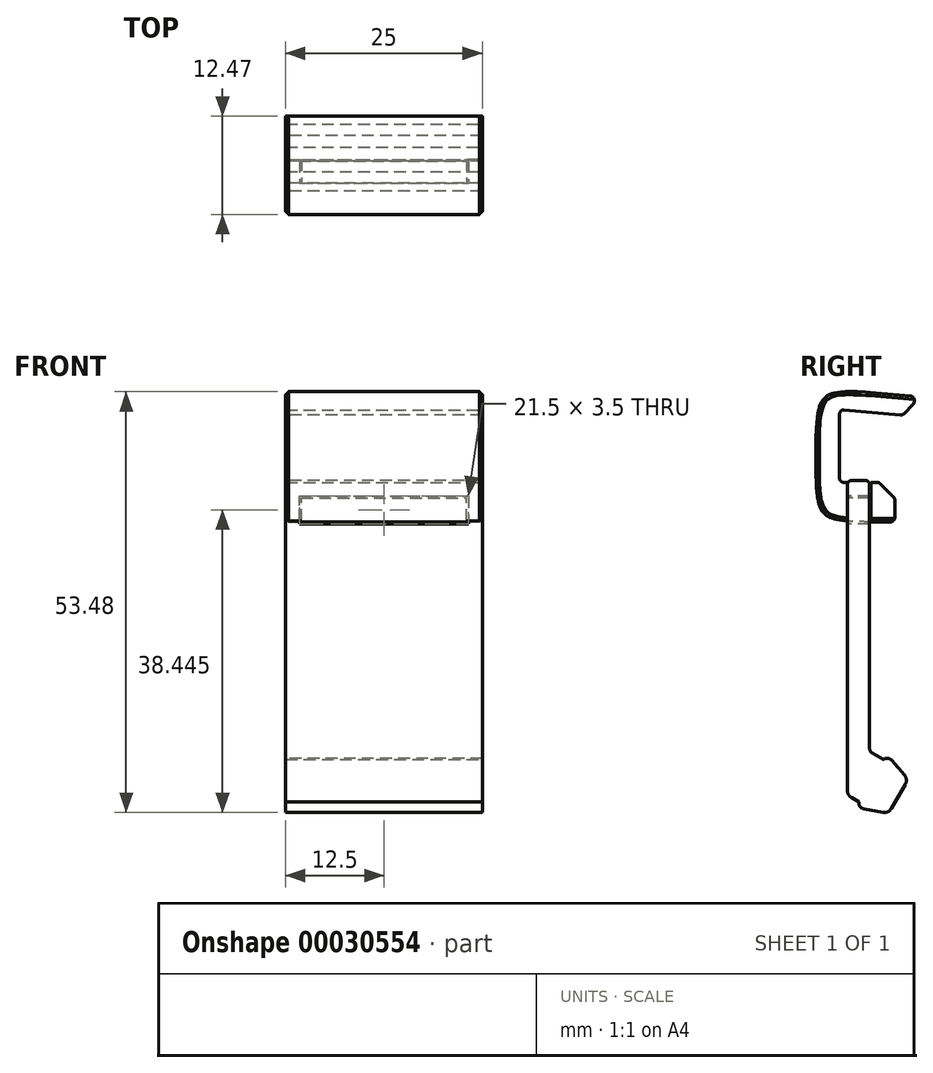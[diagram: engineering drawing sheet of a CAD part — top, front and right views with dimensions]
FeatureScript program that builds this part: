
annotation { "Feature Type Name" : "Feature", "Feature Type Description" : "" }
export const myFeature = defineFeature(function(context is Context, id is Id, definition is map)
    precondition{}
    {
        {
            var Q0;
            Q0=qCreatedBy(makeId("Right.planeOp"),FACE);
            var sketch = newSketch(context, id + "F0", { "sketchPlane" : qUnion([Q0])});
            skLineSegment(sketch, "E0", {"start": v(0, 4.62) * mm, "end": v(0, -4.62) * mm});
            skLineSegment(sketch, "E1", {"start": v(0, -4.62) * mm, "end": v(5, -4.62) * mm});
            skLineSegment(sketch, "E2", {"start": v(5, -4.62) * mm, "end": v(7, -6.62) * mm});
            skLineSegment(sketch, "E3", {"start": v(7, -6.62) * mm, "end": v(7, -9.62) * mm});
            skLineSegment(sketch, "E4", {"start": v(7, -9.62) * mm, "end": v(-3, -9.62) * mm});
            skLineSegment(sketch, "E5", {"start": v(-3, -9.63) * mm, "end": v(-3, 7.4) * mm});
            skLineSegment(sketch, "E6", {"start": v(-3, 7.4) * mm, "end": v(9.47, 6.3) * mm});
            skLineSegment(sketch, "E7", {"start": v(9.47, 6.3) * mm, "end": v(9.47, 5.43) * mm});
            skLineSegment(sketch, "E8", {"start": v(9.47, 5.43) * mm, "end": v(7.97, 3.93) * mm});
            skLineSegment(sketch, "E9", {"start": v(7.97, 3.93) * mm, "end": v(0, 4.63) * mm});
            skLineSegment(sketch, "E10", {"start": v(7.97, 3.93) * mm, "end": v(9.47, 3.93) * mm, "construction": true});
            skLineSegment(sketch, "E11", {"start": v(9.47, 3.93) * mm, "end": v(9.47, 5.43) * mm, "construction": true});
            skLineSegment(sketch, "E12", {"start": v(5, -4.62) * mm, "end": v(7, -4.62) * mm, "construction": true});
            skLineSegment(sketch, "E13", {"start": v(7, -4.62) * mm, "end": v(7, -6.62) * mm, "construction": true});
            skSolve(sketch);
        }
        {
            var Q0;
            Q0 = qSketchRegion(id + "F0", true);
            extrude(context, id + "F1", {"entities" : qUnion([Q0]), "depth" : 25 * mm});
        }
        {
            var Q0;
            Q0=makeQuery(id+"F1.opExtrude","SWEPT_EDGE",EDGE,{"disambiguationData":[OSD([sQuery(id+"F0.wireOp",EDGE,"E5"),sQuery(id+"F0.wireOp",EDGE,"E6")])]});
            var Q1;
            Q1=makeQuery(id+"F1.opExtrude","SWEPT_EDGE",EDGE,{"disambiguationData":[OSD([sQuery(id+"F0.wireOp",EDGE,"E4"),sQuery(id+"F0.wireOp",EDGE,"E5")])]});
            fillet(context, id + "F2", {"entities" : qUnion([Q0, Q1]), "radius" : 7 * mm, "tangentPropagation" : true, "rho" : .7, "crossSection" : FilletCrossSection.CONIC, "allowEdgeOverflow" : false});
        }
        {
            var Q0;
            Q0=makeQuery(id+"F1.opExtrude","SWEPT_EDGE",EDGE,{"disambiguationData":[OSD([sQuery(id+"F0.wireOp",EDGE,"E0"),sQuery(id+"F0.wireOp",EDGE,"E9")])]});
            var Q1;
            Q1=makeQuery(id+"F1.opExtrude","SWEPT_EDGE",EDGE,{"disambiguationData":[OSD([sQuery(id+"F0.wireOp",EDGE,"E0"),sQuery(id+"F0.wireOp",EDGE,"E1")])]});
            var Q2;
            Q2=makeQuery(id+"F1.opExtrude","SWEPT_EDGE",EDGE,{"disambiguationData":[OSD([sQuery(id+"F0.wireOp",EDGE,"E6"),sQuery(id+"F0.wireOp",EDGE,"E7")])]});
            var Q3;
            Q3=makeQuery(id+"F1.opExtrude","SWEPT_EDGE",EDGE,{"disambiguationData":[OSD([sQuery(id+"F0.wireOp",EDGE,"E7"),sQuery(id+"F0.wireOp",EDGE,"E8")])]});
            var Q4;
            Q4=makeQuery(id+"F1.opExtrude","SWEPT_EDGE",EDGE,{"disambiguationData":[OSD([sQuery(id+"F0.wireOp",EDGE,"E8"),sQuery(id+"F0.wireOp",EDGE,"E9")])]});
            var Q5;
            Q5=makeQuery(id+"F1.opExtrude","SWEPT_EDGE",EDGE,{"disambiguationData":[OSD([sQuery(id+"F0.wireOp",EDGE,"E1"),sQuery(id+"F0.wireOp",EDGE,"E2")])]});
            var Q6;
            Q6=makeQuery(id+"F1.opExtrude","SWEPT_EDGE",EDGE,{"disambiguationData":[OSD([sQuery(id+"F0.wireOp",EDGE,"E2"),sQuery(id+"F0.wireOp",EDGE,"E3")])]});
            var Q7;
            Q7=makeQuery(id+"F1.opExtrude","SWEPT_EDGE",EDGE,{"disambiguationData":[OSD([sQuery(id+"F0.wireOp",EDGE,"E3"),sQuery(id+"F0.wireOp",EDGE,"E4")])]});
            fillet(context, id + "F3", {"entities" : qUnion([Q0, Q1, Q2, Q3, Q4, Q5, Q6, Q7]), "radius" : .5 * mm, "tangentPropagation" : true, "allowEdgeOverflow" : false});
        }
        {
            var Q0;
            Q0=makeQuery(id+"F1.opExtrude","CAP_FACE",FACE,{"disambiguationData":[OSD([sQuery(id+"F0.wireOp",EDGE,"E0"),sQuery(id+"F0.wireOp",EDGE,"E1"),sQuery(id+"F0.wireOp",EDGE,"E2"),sQuery(id+"F0.wireOp",EDGE,"E3"),sQuery(id+"F0.wireOp",EDGE,"E4"),sQuery(id+"F0.wireOp",EDGE,"E5"),sQuery(id+"F0.wireOp",EDGE,"E6"),sQuery(id+"F0.wireOp",EDGE,"E7"),sQuery(id+"F0.wireOp",EDGE,"E8"),sQuery(id+"F0.wireOp",EDGE,"E9")])],"isStart":false});
            var sketch = newSketch(context, id + "F4", { "sketchPlane" : qUnion([Q0])});
            skLineSegment(sketch, "E14.bottom", {"start": v(1, -4.62) * mm, "end": v(4, -4.62) * mm});
            skLineSegment(sketch, "E14.top", {"start": v(1, -6.62) * mm, "end": v(4, -6.62) * mm});
            skLineSegment(sketch, "E14.left", {"start": v(1, -4.62) * mm, "end": v(1, -6.62) * mm});
            skLineSegment(sketch, "E14.right", {"start": v(4, -4.62) * mm, "end": v(4, -6.62) * mm});
            skSolve(sketch);
        }
        {
            var Q0;
            Q0 = qSketchRegion(id + "F4", true);
            extrude(context, id + "F5", {"entities" : qUnion([Q0]), "operationType" : NewBodyOperationType.REMOVE, "endBound" : BoundingType.THROUGH_ALL, "oppositeDirection" : true, "depth" : 25 * mm});
        }
        {
            var Q0;
            Q0=makeQuery(id+"F5.boolean.opBoolean","COPY",FACE,{"derivedFrom":makeQuery(id+"F5.opExtrude","SWEPT_FACE",FACE,{"disambiguationData":[OSD([sQuery(id+"F4.wireOp",EDGE,"E14.top")])]})});
            var sketch = newSketch(context, id + "F6", { "sketchPlane" : qUnion([Q0])});
            skLineSegment(sketch, "E15.bottom", {"start": v(25, 4) * mm, "end": v(23, 4) * mm});
            skLineSegment(sketch, "E15.top", {"start": v(25, 1) * mm, "end": v(23, 1) * mm});
            skLineSegment(sketch, "E15.left", {"start": v(25, 4) * mm, "end": v(25, 1) * mm});
            skLineSegment(sketch, "E15.right", {"start": v(23, 4) * mm, "end": v(23, 1) * mm});
            skLineSegment(sketch, "E16.bottom", {"start": v(0, 1) * mm, "end": v(2, 1) * mm});
            skLineSegment(sketch, "E16.top", {"start": v(0, 4) * mm, "end": v(2, 4) * mm});
            skLineSegment(sketch, "E16.left", {"start": v(0, 4) * mm, "end": v(0, 1) * mm});
            skLineSegment(sketch, "E16.right", {"start": v(2, 4) * mm, "end": v(2, 1) * mm});
            skSolve(sketch);
        }
        {
            var Q0;
            Q0 = qSketchRegion(id + "F6", true);
            extrude(context, id + "F7", {"entities" : qUnion([Q0]), "operationType" : NewBodyOperationType.REMOVE, "endBound" : BoundingType.UP_TO_NEXT, "oppositeDirection" : true, "depth" : 25 * mm});
        }
        {
            var Q0;
            Q0=makeQuery(id+"F7.boolean.opBoolean","MERGE",FACE,{"derivedFrom":[makeQuery(id+"F5.boolean.opBoolean","COPY",FACE,{"derivedFrom":makeQuery(id+"F5.opExtrude","SWEPT_FACE",FACE,{"disambiguationData":[OSD([sQuery(id+"F4.wireOp",EDGE,"E14.left")])]})}),makeQuery(id+"F5.boolean.opBoolean","COPY",FACE,{"derivedFrom":makeQuery(id+"F5.opExtrude","SWEPT_FACE",FACE,{"disambiguationData":[OSD([sQuery(id+"F4.wireOp",EDGE,"d3d7cda7-cd1c-4aa4-936c-d04dcb39f244.right")])]})}),makeQuery(id+"F7.opExtrude","SWEPT_FACE",FACE,{"disambiguationData":[OSD([sQuery(id+"F6.wireOp",EDGE,"E15.bottom")])]}),makeQuery(id+"F7.opExtrude","SWEPT_FACE",FACE,{"disambiguationData":[OSD([sQuery(id+"F6.wireOp",EDGE,"E16.bottom")])]})]});
            cPlane(context, id + "F8", {"entities" : qUnion([Q0]), "cplaneType" : CPlaneType.OFFSET, "offset" : 0 * mm, "width" : 150 * mm, "height" : 150 * mm});
        }
        {
            var Q0;
            Q0=qCreatedBy(id+"F8.planeOp",FACE);
            var sketch = newSketch(context, id + "F9", { "sketchPlane" : qUnion([Q0])});
            skLineSegment(sketch, "E17.bottom", {"start": v(-25, -4.37) * mm, "end": v(0, -4.37) * mm});
            skLineSegment(sketch, "E17.top", {"start": v(-25, -44.38) * mm, "end": v(0, -44.38) * mm});
            skLineSegment(sketch, "E17.left", {"start": v(-25, -4.38) * mm, "end": v(-25, -44.38) * mm});
            skLineSegment(sketch, "E17.right", {"start": v(0, -4.37) * mm, "end": v(0, -44.38) * mm});
            skLineSegment(sketch, "E18.1", {"start": v(-2, -6.62) * mm, "end": v(-23, -6.62) * mm, "construction": true});
            skLineSegment(sketch, "E18.2", {"start": v(-2, -6.63) * mm, "end": v(-2, -6.63) * mm});
            skLineSegment(sketch, "E19", {"start": v(-23, -6.63) * mm, "end": v(-23, -9.63) * mm, "construction": true});
            skLineSegment(sketch, "E20", {"start": v(-23, -9.63) * mm, "end": v(-2, -9.63) * mm, "construction": true});
            skLineSegment(sketch, "E21", {"start": v(-2, -9.63) * mm, "end": v(-2, -6.62) * mm, "construction": true});
            skLineSegment(sketch, "E22.0", {"start": v(-1.75, -6.37) * mm, "end": v(-23.25, -6.37) * mm});
            skLineSegment(sketch, "E22.1", {"start": v(-1.75, -9.88) * mm, "end": v(-1.75, -6.37) * mm});
            skLineSegment(sketch, "E22.2", {"start": v(-23.25, -9.88) * mm, "end": v(-1.75, -9.88) * mm});
            skLineSegment(sketch, "E22.3", {"start": v(-23.25, -6.37) * mm, "end": v(-23.25, -9.88) * mm});
            skSolve(sketch);
        }
        {
            var Q0;
            Q0 = qSketchRegion(id + "F9", true);
            extrude(context, id + "F10", {"entities" : qUnion([Q0]), "depth" : 2.8 * mm});
        }
        {
            var Q0;
            Q0=makeQuery(id+"F10.opExtrude","CAP_EDGE",EDGE,{"disambiguationData":[OSD([sQuery(id+"F9.wireOp",EDGE,"E17.bottom")])],"isStart":false});
            var Q1;
            Q1=makeQuery(id+"F10.opExtrude","CAP_EDGE",EDGE,{"disambiguationData":[OSD([sQuery(id+"F9.wireOp",EDGE,"E17.bottom")])],"isStart":true});
            fillet(context, id + "F11", {"entities" : qUnion([Q0, Q1]), "radius" : .5 * mm, "tangentPropagation" : true, "allowEdgeOverflow" : false});
        }
        {
            var Q0;
            Q0=makeQuery(id+"F10.opExtrude","SWEPT_FACE",FACE,{"disambiguationData":[OSD([sQuery(id+"F9.wireOp",EDGE,"E17.left")])]});
            var sketch = newSketch(context, id + "F12", { "sketchPlane" : qUnion([Q0])});
            skLineSegment(sketch, "E23", {"start": v(5.93, -39.14) * mm, "end": v(8.7, -42.35) * mm});
            skLineSegment(sketch, "E24", {"start": v(8.7, -42.35) * mm, "end": v(6.2, -46.68) * mm});
            skLineSegment(sketch, "E25", {"start": v(6.2, -46.68) * mm, "end": v(2.03, -45.9) * mm});
            skLineSegment(sketch, "E26", {"start": v(2.03, -45.9) * mm, "end": v(2.43, -45.2) * mm});
            skLineSegment(sketch, "E27", {"start": v(2.43, -45.2) * mm, "end": v(1, -44.38) * mm});
            skLineSegment(sketch, "E28", {"start": v(1, -44.38) * mm, "end": v(1, -37.22) * mm});
            skLineSegment(sketch, "E29", {"start": v(1, -37.22) * mm, "end": v(5.53, -39.83) * mm});
            skLineSegment(sketch, "E30", {"start": v(5.53, -39.83) * mm, "end": v(5.93, -39.14) * mm});
            skPoint(sketch, "E31", {"position": v(3.8, -38.83) * mm});
            skSolve(sketch);
        }
        {
            var Q0;
            Q0 = qSketchRegion(id + "F12", true);
            var Q1;
            Q1=makeQuery(id+"F10.opExtrude","SWEPT_FACE",FACE,{"disambiguationData":[OSD([sQuery(id+"F9.wireOp",EDGE,"E17.right")])]});
            extrude(context, id + "F13", {"entities" : qUnion([Q0]), "operationType" : NewBodyOperationType.ADD, "endBound" : BoundingType.UP_TO_SURFACE, "oppositeDirection" : true, "endBoundEntityFace" : qUnion([Q1]), "depth" : 25 * mm});
        }
        {
            var Q0;
            {var subQ0=sQuery(id+"F9.wireOp",EDGE,"E17.top");Q0=makeQuery(id+"F13.boolean.opBoolean","MERGE",EDGE,{"derivedFrom":[makeQuery(id+"F10.opExtrude","CAP_EDGE",EDGE,{"disambiguationData":[OSD([subQ0])],"isStart":true}),makeQuery(id+"F13.opExtrude","SWEPT_EDGE",EDGE,{"disambiguationData":[OSD([subQ0,sQuery(id+"F9.wireOp",EDGE,"E17.left"),sQuery(id+"F12.wireOp",EDGE,"E27"),sQuery(id+"F12.wireOp",EDGE,"E28")])]})]});}
            var Q1;
            Q1=makeQuery(id+"F13.opExtrude","SWEPT_EDGE",EDGE,{"disambiguationData":[OSD([sQuery(id+"F12.wireOp",EDGE,"E23"),sQuery(id+"F12.wireOp",EDGE,"E24")])]});
            var Q2;
            Q2=makeQuery(id+"F13.opExtrude","SWEPT_EDGE",EDGE,{"disambiguationData":[OSD([sQuery(id+"F12.wireOp",EDGE,"E24"),sQuery(id+"F12.wireOp",EDGE,"E25")])]});
            fillet(context, id + "F14", {"entities" : qUnion([Q0, Q1, Q2]), "radius" : 1 * mm, "tangentPropagation" : true, "allowEdgeOverflow" : false});
        }
        {
            var Q0;
            Q0=makeQuery(id+"F13.opExtrude","SWEPT_EDGE",EDGE,{"disambiguationData":[OSD([sQuery(id+"F12.wireOp",EDGE,"E23"),sQuery(id+"F12.wireOp",EDGE,"E30")])]});
            var Q1;
            Q1=makeQuery(id+"F13.opExtrude","SWEPT_EDGE",EDGE,{"disambiguationData":[OSD([sQuery(id+"F12.wireOp",EDGE,"E25"),sQuery(id+"F12.wireOp",EDGE,"E26")])]});
            var Q2;
            Q2=makeQuery(id+"F13.boolean.opBoolean","INTERSECT",EDGE,{"derivedFrom":[makeQuery(id+"F10.opExtrude","CAP_FACE",FACE,{"disambiguationData":[OSD([sQuery(id+"F9.wireOp",EDGE,"E17.bottom"),sQuery(id+"F9.wireOp",EDGE,"E17.top"),sQuery(id+"F9.wireOp",EDGE,"E17.left"),sQuery(id+"F9.wireOp",EDGE,"E17.right"),sQuery(id+"F9.wireOp",EDGE,"E22.0"),sQuery(id+"F9.wireOp",EDGE,"E22.1"),sQuery(id+"F9.wireOp",EDGE,"E22.2"),sQuery(id+"F9.wireOp",EDGE,"E22.3")])],"isStart":false}),makeQuery(id+"F13.opExtrude","SWEPT_FACE",FACE,{"disambiguationData":[OSD([sQuery(id+"F12.wireOp",EDGE,"E29")])]})]});
            fillet(context, id + "F15", {"entities" : qUnion([Q0, Q1, Q2]), "radius" : .8 * mm, "tangentPropagation" : true, "allowEdgeOverflow" : false});
        }
        {
            var Q0;
            Q0=makeQuery(id+"F1.opExtrude","CAP_EDGE",EDGE,{"disambiguationData":[OSD([sQuery(id+"F0.wireOp",EDGE,"E6")])],"isStart":false});
            var Q1;
            {var subQ0=sQuery(id+"F0.wireOp",EDGE,"E5");var subQ1=sQuery(id+"F0.wireOp",EDGE,"E6");Q1=makeQuery(id+"F2.opFillet","BLEND_EDGE",EDGE,{"blendedFrom":[makeQuery(id+"F1.opExtrude","SWEPT_EDGE",EDGE,{"disambiguationData":[OSD([subQ0,subQ1])]}),makeQuery(id+"F1.opExtrude","CAP_FACE",FACE,{"disambiguationData":[OSD([sQuery(id+"F0.wireOp",EDGE,"E0"),sQuery(id+"F0.wireOp",EDGE,"E1"),sQuery(id+"F0.wireOp",EDGE,"E2"),sQuery(id+"F0.wireOp",EDGE,"E3"),sQuery(id+"F0.wireOp",EDGE,"E4"),subQ0,subQ1,sQuery(id+"F0.wireOp",EDGE,"E7"),sQuery(id+"F0.wireOp",EDGE,"E8"),sQuery(id+"F0.wireOp",EDGE,"E9")])],"isStart":false})],"blendedInto":[makeQuery(id+"F1.opExtrude","CAP_FACE",FACE,{"disambiguationData":[OSD([sQuery(id+"F0.wireOp",EDGE,"E0"),sQuery(id+"F0.wireOp",EDGE,"E1"),sQuery(id+"F0.wireOp",EDGE,"E2"),sQuery(id+"F0.wireOp",EDGE,"E3"),sQuery(id+"F0.wireOp",EDGE,"E4"),subQ0,subQ1,sQuery(id+"F0.wireOp",EDGE,"E7"),sQuery(id+"F0.wireOp",EDGE,"E8"),sQuery(id+"F0.wireOp",EDGE,"E9")])],"isStart":false})]});}
            var Q2;
            {var subQ0=sQuery(id+"F0.wireOp",EDGE,"E4");var subQ1=sQuery(id+"F0.wireOp",EDGE,"E5");Q2=makeQuery(id+"F2.opFillet","BLEND_EDGE",EDGE,{"blendedFrom":[makeQuery(id+"F1.opExtrude","SWEPT_EDGE",EDGE,{"disambiguationData":[OSD([subQ0,subQ1])]}),makeQuery(id+"F1.opExtrude","CAP_FACE",FACE,{"disambiguationData":[OSD([sQuery(id+"F0.wireOp",EDGE,"E0"),sQuery(id+"F0.wireOp",EDGE,"E1"),sQuery(id+"F0.wireOp",EDGE,"E2"),sQuery(id+"F0.wireOp",EDGE,"E3"),subQ0,subQ1,sQuery(id+"F0.wireOp",EDGE,"E6"),sQuery(id+"F0.wireOp",EDGE,"E7"),sQuery(id+"F0.wireOp",EDGE,"E8"),sQuery(id+"F0.wireOp",EDGE,"E9")])],"isStart":false})],"blendedInto":[makeQuery(id+"F1.opExtrude","CAP_FACE",FACE,{"disambiguationData":[OSD([sQuery(id+"F0.wireOp",EDGE,"E0"),sQuery(id+"F0.wireOp",EDGE,"E1"),sQuery(id+"F0.wireOp",EDGE,"E2"),sQuery(id+"F0.wireOp",EDGE,"E3"),subQ0,subQ1,sQuery(id+"F0.wireOp",EDGE,"E6"),sQuery(id+"F0.wireOp",EDGE,"E7"),sQuery(id+"F0.wireOp",EDGE,"E8"),sQuery(id+"F0.wireOp",EDGE,"E9")])],"isStart":false})]});}
            var Q3;
            Q3=makeQuery(id+"F1.opExtrude","CAP_EDGE",EDGE,{"disambiguationData":[OSD([sQuery(id+"F0.wireOp",EDGE,"E4")])],"isStart":false});
            var Q4;
            Q4=makeQuery(id+"F1.opExtrude","CAP_EDGE",EDGE,{"disambiguationData":[OSD([sQuery(id+"F0.wireOp",EDGE,"E6")])],"isStart":true});
            var Q5;
            {var subQ0=sQuery(id+"F0.wireOp",EDGE,"E5");var subQ1=sQuery(id+"F0.wireOp",EDGE,"E6");Q5=makeQuery(id+"F2.opFillet","BLEND_EDGE",EDGE,{"blendedFrom":[makeQuery(id+"F1.opExtrude","SWEPT_EDGE",EDGE,{"disambiguationData":[OSD([subQ0,subQ1])]}),makeQuery(id+"F1.opExtrude","CAP_FACE",FACE,{"disambiguationData":[OSD([sQuery(id+"F0.wireOp",EDGE,"E0"),sQuery(id+"F0.wireOp",EDGE,"E1"),sQuery(id+"F0.wireOp",EDGE,"E2"),sQuery(id+"F0.wireOp",EDGE,"E3"),sQuery(id+"F0.wireOp",EDGE,"E4"),subQ0,subQ1,sQuery(id+"F0.wireOp",EDGE,"E7"),sQuery(id+"F0.wireOp",EDGE,"E8"),sQuery(id+"F0.wireOp",EDGE,"E9")])],"isStart":true})],"blendedInto":[makeQuery(id+"F1.opExtrude","CAP_FACE",FACE,{"disambiguationData":[OSD([sQuery(id+"F0.wireOp",EDGE,"E0"),sQuery(id+"F0.wireOp",EDGE,"E1"),sQuery(id+"F0.wireOp",EDGE,"E2"),sQuery(id+"F0.wireOp",EDGE,"E3"),sQuery(id+"F0.wireOp",EDGE,"E4"),subQ0,subQ1,sQuery(id+"F0.wireOp",EDGE,"E7"),sQuery(id+"F0.wireOp",EDGE,"E8"),sQuery(id+"F0.wireOp",EDGE,"E9")])],"isStart":true})]});}
            var Q6;
            Q6=makeQuery(id+"F1.opExtrude","CAP_EDGE",EDGE,{"disambiguationData":[OSD([sQuery(id+"F0.wireOp",EDGE,"E5")])],"isStart":true});
            var Q7;
            {var subQ0=sQuery(id+"F0.wireOp",EDGE,"E4");var subQ1=sQuery(id+"F0.wireOp",EDGE,"E5");Q7=makeQuery(id+"F2.opFillet","BLEND_EDGE",EDGE,{"blendedFrom":[makeQuery(id+"F1.opExtrude","SWEPT_EDGE",EDGE,{"disambiguationData":[OSD([subQ0,subQ1])]}),makeQuery(id+"F1.opExtrude","CAP_FACE",FACE,{"disambiguationData":[OSD([sQuery(id+"F0.wireOp",EDGE,"E0"),sQuery(id+"F0.wireOp",EDGE,"E1"),sQuery(id+"F0.wireOp",EDGE,"E2"),sQuery(id+"F0.wireOp",EDGE,"E3"),subQ0,subQ1,sQuery(id+"F0.wireOp",EDGE,"E6"),sQuery(id+"F0.wireOp",EDGE,"E7"),sQuery(id+"F0.wireOp",EDGE,"E8"),sQuery(id+"F0.wireOp",EDGE,"E9")])],"isStart":true})],"blendedInto":[makeQuery(id+"F1.opExtrude","CAP_FACE",FACE,{"disambiguationData":[OSD([sQuery(id+"F0.wireOp",EDGE,"E0"),sQuery(id+"F0.wireOp",EDGE,"E1"),sQuery(id+"F0.wireOp",EDGE,"E2"),sQuery(id+"F0.wireOp",EDGE,"E3"),subQ0,subQ1,sQuery(id+"F0.wireOp",EDGE,"E6"),sQuery(id+"F0.wireOp",EDGE,"E7"),sQuery(id+"F0.wireOp",EDGE,"E8"),sQuery(id+"F0.wireOp",EDGE,"E9")])],"isStart":true})]});}
            var Q8;
            Q8=makeQuery(id+"F1.opExtrude","CAP_EDGE",EDGE,{"disambiguationData":[OSD([sQuery(id+"F0.wireOp",EDGE,"E4")])],"isStart":true});
            chamfer(context, id + "F16", {"entities" : qUnion([Q0, Q1, Q2, Q3, Q4, Q5, Q6, Q7, Q8]), "width" : .4 * mm});
        }
    });
